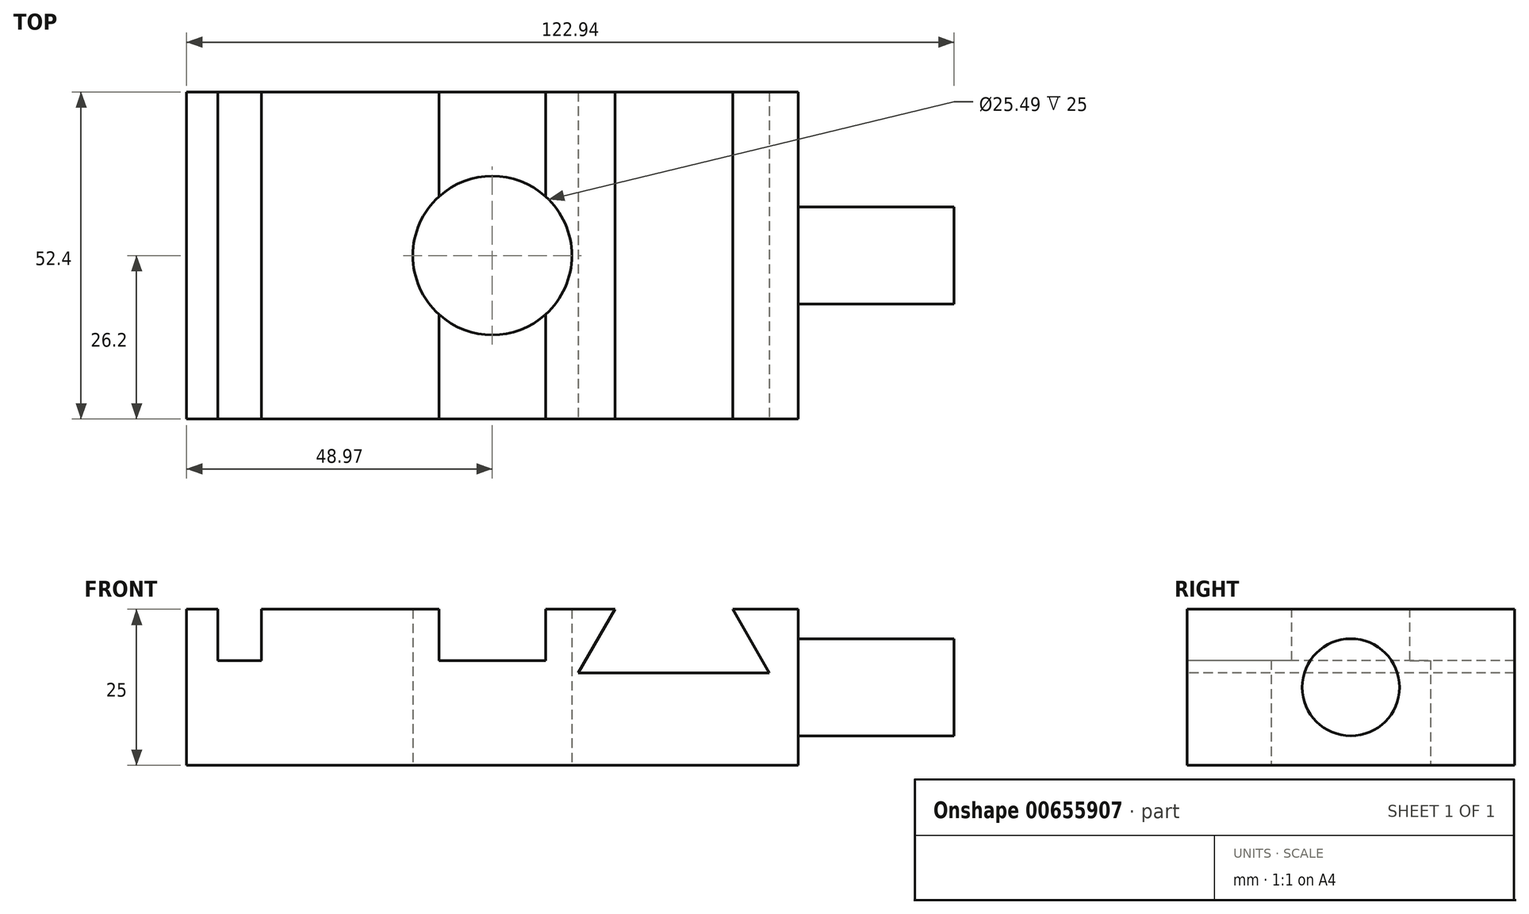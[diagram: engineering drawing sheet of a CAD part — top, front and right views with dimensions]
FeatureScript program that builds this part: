
annotation { "Feature Type Name" : "Feature", "Feature Type Description" : "" }
export const myFeature = defineFeature(function(context is Context, id is Id, definition is map)
    precondition{}
    {
        {
            var Q0;
            Q0=qCreatedBy(makeId("Top.planeOp"),FACE);
            var sketch = newSketch(context, id + "F0", { "sketchPlane" : qUnion([Q0])});
            skLineSegment(sketch, "E0.bottom", {"start": v(-48.97, 26.2) * mm, "end": v(48.97, 26.2) * mm});
            skLineSegment(sketch, "E0.top", {"start": v(-48.97, -26.2) * mm, "end": v(48.97, -26.2) * mm});
            skLineSegment(sketch, "E0.left", {"start": v(-48.97, 26.2) * mm, "end": v(-48.97, -26.2) * mm});
            skLineSegment(sketch, "E0.right", {"start": v(48.97, 26.2) * mm, "end": v(48.97, -26.2) * mm});
            skPoint(sketch, "E0.middle", {"position": v(0, 0) * mm});
            skCircle(sketch, "E1", {"center": v(0, 0) * mm, "radius": 12.75 * mm});
            skSolve(sketch);
        }
        {
            var Q0;
            Q0=makeQuery(id+"F0.imprint","IMPRINT",FACE,{"disambiguationData":[TD([[makeQuery(id+"F0.imprint","IMPRINT",EDGE,{"derivedFrom":sQuery(id+"F0.wireOp",EDGE,"E0.bottom")}),-1.0]])]});
            extrude(context, id + "F1", {"entities" : qUnion([Q0]), "depth" : 25 * mm, "offsetDistance" : 25 * mm});
        }
        {
            var Q0;
            Q0=makeQuery(id+"F1.opExtrude","CAP_FACE",FACE,{"disambiguationData":[OSD([sQuery(id+"F0.wireOp",EDGE,"E0.bottom"),sQuery(id+"F0.wireOp",EDGE,"E0.top"),sQuery(id+"F0.wireOp",EDGE,"E0.left"),sQuery(id+"F0.wireOp",EDGE,"E0.right"),sQuery(id+"F0.wireOp",EDGE,"E1")])],"isStart":false});
            var sketch = newSketch(context, id + "F2", { "sketchPlane" : qUnion([Q0])});
            skLineSegment(sketch, "E2.bottom", {"start": v(-48.97, 26.2) * mm, "end": v(-43.97, 26.2) * mm});
            skLineSegment(sketch, "E2.top", {"start": v(-48.97, -26.2) * mm, "end": v(-43.97, -26.2) * mm});
            skLineSegment(sketch, "E2.left", {"start": v(-48.97, 26.2) * mm, "end": v(-48.97, -26.2) * mm});
            skLineSegment(sketch, "E2.right", {"start": v(-43.97, 26.2) * mm, "end": v(-43.97, -26.2) * mm});
            skLineSegment(sketch, "E3.bottom", {"start": v(-43.97, 26.2) * mm, "end": v(-36.97, 26.2) * mm});
            skLineSegment(sketch, "E3.top", {"start": v(-43.97, -26.2) * mm, "end": v(-36.97, -26.2) * mm});
            skLineSegment(sketch, "E3.right", {"start": v(-36.97, 26.2) * mm, "end": v(-36.97, -26.2) * mm});
            skLineSegment(sketch, "E4", {"start": v(-8.55, 26.2) * mm, "end": v(-8.55, -26.2) * mm});
            skLineSegment(sketch, "E5", {"start": v(-8.55, -26.2) * mm, "end": v(8.55, -26.2) * mm});
            skLineSegment(sketch, "E6", {"start": v(8.55, -26.2) * mm, "end": v(8.55, 26.2) * mm});
            skLineSegment(sketch, "E7", {"start": v(8.55, 26.2) * mm, "end": v(-8.55, 26.2) * mm});
            skLineSegment(sketch, "E8", {"start": v(0, 26.2) * mm, "end": v(0, -26.2) * mm, "construction": true});
            skSolve(sketch);
        }
        {
            var Q0;
            Q0=makeQuery(id+"F2.imprint","IMPRINT",FACE,{"disambiguationData":[TD([[makeQuery(id+"F2.imprint","IMPRINT",EDGE,{"derivedFrom":sQuery(id+"F2.wireOp",EDGE,"E3.bottom")}),-1.0]])]});
            var Q1;
            {var subQ0=sQuery(id+"F2.wireOp",EDGE,"E7");Q1=makeQuery(id+"F2.imprint","IMPRINT",FACE,{"disambiguationData":[TD([[makeQuery(id+"F2.imprint","IMPRINT",EDGE,{"derivedFrom":subQ0}),-1.0]])]});}
            var Q2;
            {var subQ0=sQuery(id+"F2.wireOp",EDGE,"E5");Q2=makeQuery(id+"F2.imprint","IMPRINT",FACE,{"disambiguationData":[TD([[makeQuery(id+"F2.imprint","IMPRINT",EDGE,{"derivedFrom":subQ0}),1.0]])]});}
            extrude(context, id + "F3", {"entities" : qUnion([Q0, Q1, Q2]), "operationType" : NewBodyOperationType.REMOVE, "oppositeDirection" : true, "depth" : 8.2 * mm, "offsetDistance" : 25 * mm});
        }
        {
            var Q0;
            Q0=makeQuery(id+"F1.opExtrude","SWEPT_FACE",FACE,{"disambiguationData":[OSD([sQuery(id+"F0.wireOp",EDGE,"E0.top")])]});
            var sketch = newSketch(context, id + "F4", { "sketchPlane" : qUnion([Q0])});
            skLineSegment(sketch, "E9", {"start": v(19.64, 25) * mm, "end": v(13.77, 14.83) * mm});
            skLineSegment(sketch, "E10", {"start": v(13.77, 14.83) * mm, "end": v(44.37, 14.83) * mm});
            skLineSegment(sketch, "E11", {"start": v(44.37, 14.83) * mm, "end": v(38.5, 25) * mm});
            skLineSegment(sketch, "E12", {"start": v(38.5, 25) * mm, "end": v(19.64, 25) * mm});
            skLineSegment(sketch, "E13", {"start": v(29.07, 14.83) * mm, "end": v(29.07, 25) * mm, "construction": true});
            skSolve(sketch);
        }
        {
            var Q0;
            Q0=makeQuery(id+"F4.imprint","IMPRINT",FACE,{"disambiguationData":[TD([[makeQuery(id+"F4.imprint","IMPRINT",EDGE,{"derivedFrom":sQuery(id+"F4.wireOp",EDGE,"E9")}),1.0]])]});
            extrude(context, id + "F5", {"entities" : qUnion([Q0]), "operationType" : NewBodyOperationType.REMOVE, "oppositeDirection" : true, "depth" : 55 * mm, "offsetDistance" : 25 * mm});
        }
        {
            var Q0;
            Q0=makeQuery(id+"F1.opExtrude","SWEPT_FACE",FACE,{"disambiguationData":[OSD([sQuery(id+"F0.wireOp",EDGE,"E0.right")])]});
            var sketch = newSketch(context, id + "F6", { "sketchPlane" : qUnion([Q0])});
            skCircle(sketch, "E14", {"center": v(0, 12.5) * mm, "radius": 7.78 * mm});
            skPoint(sketch, "E14.centerSnap0", {"position": v(-26.2, 12.5) * mm});
            skPoint(sketch, "E14.centerSnap1", {"position": v(0, 25) * mm});
            skSolve(sketch);
        }
        {
            var Q0;
            Q0=makeQuery(id+"F6.imprint","IMPRINT",FACE,{"disambiguationData":[TD([[makeQuery(id+"F6.imprint","IMPRINT",EDGE,{"derivedFrom":sQuery(id+"F6.wireOp",EDGE,"E14")}),1.0]])]});
            extrude(context, id + "F7", {"entities" : qUnion([Q0]), "operationType" : NewBodyOperationType.ADD, "depth" : 25 * mm, "offsetDistance" : 25 * mm});
        }
    });
